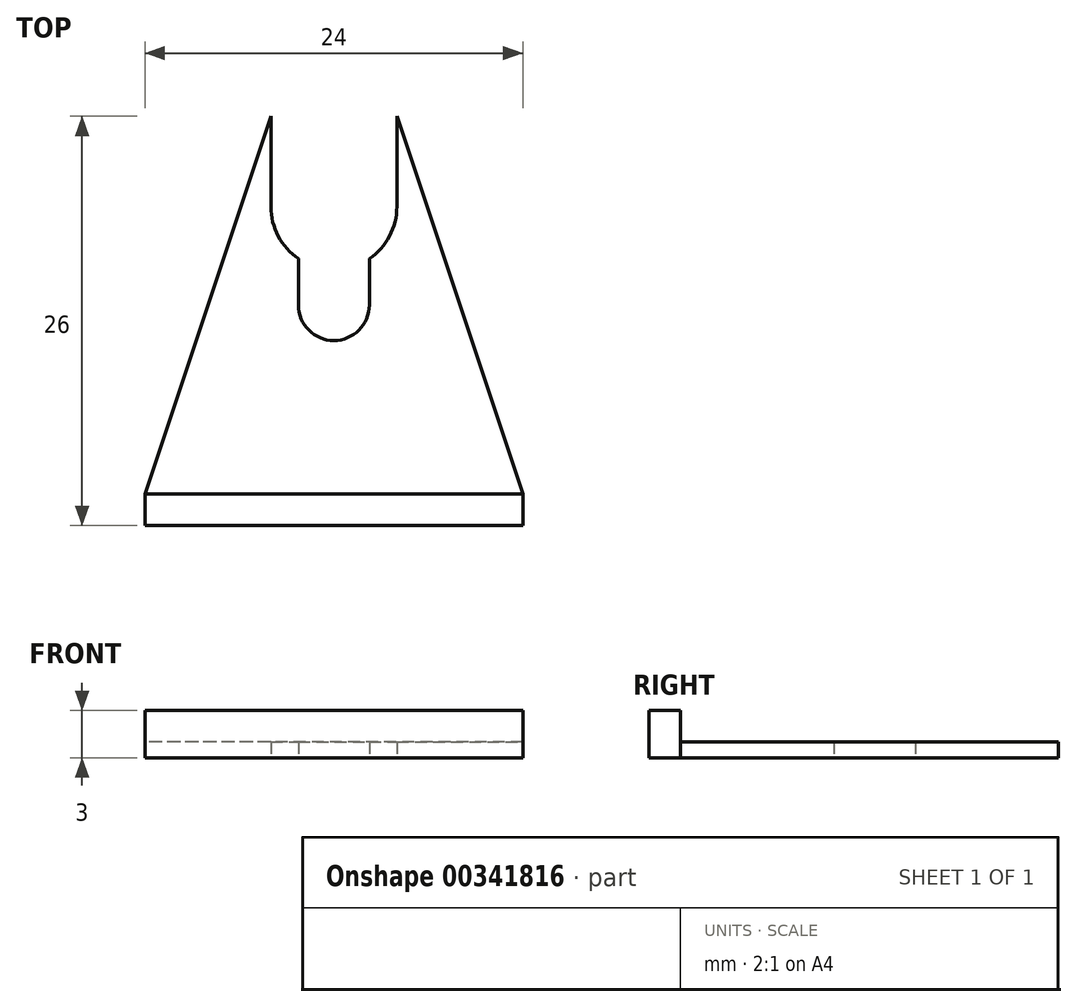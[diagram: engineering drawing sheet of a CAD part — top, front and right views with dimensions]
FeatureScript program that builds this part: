
annotation { "Feature Type Name" : "Feature", "Feature Type Description" : "" }
export const myFeature = defineFeature(function(context is Context, id is Id, definition is map)
    precondition{}
    {
        {
            var Q0;
            Q0=qCreatedBy(makeId("Top.planeOp"),FACE);
            var sketch = newSketch(context, id + "F0", { "sketchPlane" : qUnion([Q0])});
            skLineSegment(sketch, "E0.bottom", {"start": v(12, 0) * mm, "end": v(-12, 0) * mm});
            skLineSegment(sketch, "E0.top", {"start": v(12, -2) * mm, "end": v(-12, -2) * mm});
            skLineSegment(sketch, "E0.left", {"start": v(12, 0) * mm, "end": v(12, -2) * mm});
            skLineSegment(sketch, "E0.right", {"start": v(-12, 0) * mm, "end": v(-12, -2) * mm});
            skPoint(sketch, "E0.middle", {"position": v(0, -1) * mm});
            skLineSegment(sketch, "E1", {"start": v(-2.25, 12) * mm, "end": v(-2.25, 14.94) * mm});
            skLineSegment(sketch, "E2", {"start": v(2.25, 12) * mm, "end": v(2.25, 14.94) * mm});
            skLineSegment(sketch, "E3", {"start": v(4, 18.25) * mm, "end": v(4, 24) * mm});
            skLineSegment(sketch, "E4", {"start": v(-4, 18.25) * mm, "end": v(-4, 24) * mm});
            skLineSegment(sketch, "E5", {"start": v(-4, 24) * mm, "end": v(-12, 0) * mm});
            skLineSegment(sketch, "E6", {"start": v(4, 24) * mm, "end": v(12, 0) * mm});
            skArc(sketch, "E7", {"start": v(-4, 18.25) * mm, "mid": v(-3.54, 16.38) * mm, "end": v(-2.25, 14.94) * mm});
            skArc(sketch, "E8", {"start": v(4, 18.25) * mm, "mid": v(0, 22.25) * mm, "end": v(-4, 18.25) * mm, "construction": true});
            skArc(sketch, "E9", {"start": v(2.25, 14.94) * mm, "mid": v(3.54, 16.38) * mm, "end": v(4, 18.25) * mm});
            skArc(sketch, "E10", {"start": v(-2.25, 14.94) * mm, "mid": v(0, 14.25) * mm, "end": v(2.25, 14.94) * mm, "construction": true});
            skArc(sketch, "E11", {"start": v(-2.25, 12) * mm, "mid": v(0, 9.75) * mm, "end": v(2.25, 12) * mm});
            skArc(sketch, "E12", {"start": v(2.25, 12) * mm, "mid": v(0, 14.25) * mm, "end": v(-2.25, 12) * mm, "construction": true});
            skSolve(sketch);
        }
        {
            var Q0;
            Q0=makeQuery(id+"F0.imprint","IMPRINT",FACE,{"disambiguationData":[TD([[makeQuery(id+"F0.imprint","IMPRINT",EDGE,{"derivedFrom":sQuery(id+"F0.wireOp",EDGE,"E0.bottom")}),-1.0]])]});
            extrude(context, id + "F1", {"entities" : qUnion([Q0]), "depth" : 1 * mm});
        }
        {
            var Q0;
            Q0=makeQuery(id+"F0.imprint","IMPRINT",FACE,{"disambiguationData":[TD([[makeQuery(id+"F0.imprint","IMPRINT",EDGE,{"derivedFrom":sQuery(id+"F0.wireOp",EDGE,"E0.bottom")}),1.0]])]});
            extrude(context, id + "F2", {"entities" : qUnion([Q0]), "operationType" : NewBodyOperationType.ADD, "depth" : 3 * mm});
        }
    });
